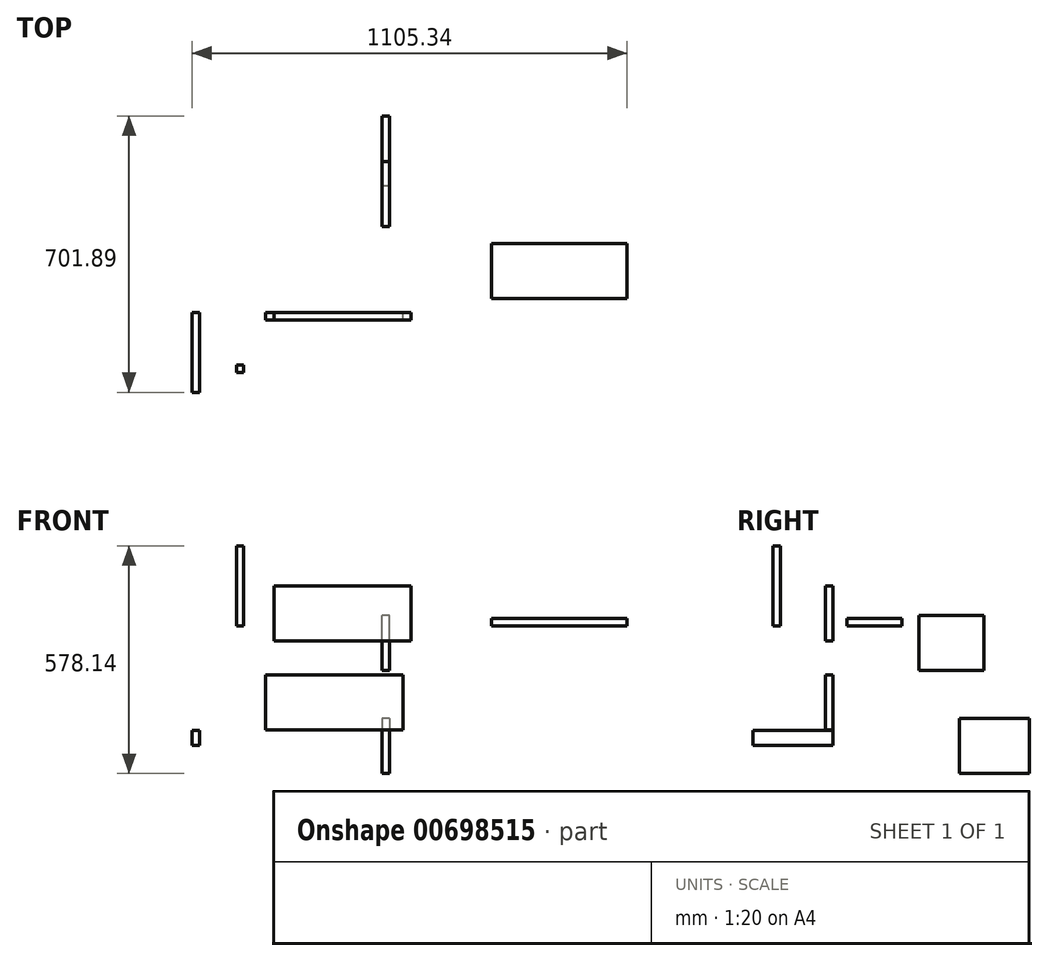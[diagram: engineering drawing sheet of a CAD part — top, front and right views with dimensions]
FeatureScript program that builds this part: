
annotation { "Feature Type Name" : "Feature", "Feature Type Description" : "" }
export const myFeature = defineFeature(function(context is Context, id is Id, definition is map)
    precondition{}
    {
        {
            var Q0;
            Q0=qCreatedBy(makeId("Front.planeOp"),FACE);
            var sketch = newSketch(context, id + "F0", { "sketchPlane" : qUnion([Q0])});
            skLineSegment(sketch, "E0.bottom", {"start": v(-274.43, 101.19) * mm, "end": v(74.34, 101.19) * mm});
            skLineSegment(sketch, "E0.top", {"start": v(-274.43, -38.51) * mm, "end": v(74.34, -38.51) * mm});
            skLineSegment(sketch, "E0.left", {"start": v(-274.43, 101.19) * mm, "end": v(-274.43, -38.51) * mm});
            skLineSegment(sketch, "E0.right", {"start": v(74.34, 101.19) * mm, "end": v(74.34, -38.51) * mm});
            skSolve(sketch);
        }
        {
            var Q0;
            Q0=makeQuery(id+"F0.imprint","IMPRINT",FACE,{"disambiguationData":[TD([[makeQuery(id+"F0.imprint","IMPRINT",EDGE,{"derivedFrom":sQuery(id+"F0.wireOp",EDGE,"E0.bottom")}),-1.0]])]});
            extrude(context, id + "F1", {"entities" : qUnion([Q0]), "depth" : 19.05 * mm, "offsetDistance" : 25.4 * mm});
        }
        {
            var Q0;
            Q0=qCreatedBy(makeId("Front.planeOp"),FACE);
            var sketch = newSketch(context, id + "F2", { "sketchPlane" : qUnion([Q0])});
            skLineSegment(sketch, "E1.bottom", {"start": v(-295.47, -125.17) * mm, "end": v(53.05, -125.17) * mm});
            skLineSegment(sketch, "E1.top", {"start": v(-295.47, -264.87) * mm, "end": v(53.05, -264.87) * mm});
            skLineSegment(sketch, "E1.left", {"start": v(-295.47, -125.17) * mm, "end": v(-295.47, -264.87) * mm});
            skLineSegment(sketch, "E1.right", {"start": v(53.05, -125.17) * mm, "end": v(53.05, -264.87) * mm});
            skSolve(sketch);
        }
        {
            var Q0;
            Q0=makeQuery(id+"F2.imprint","IMPRINT",FACE,{"disambiguationData":[TD([[makeQuery(id+"F2.imprint","IMPRINT",EDGE,{"derivedFrom":sQuery(id+"F2.wireOp",EDGE,"E1.bottom")}),-1.0]])]});
            extrude(context, id + "F3", {"entities" : qUnion([Q0]), "depth" : 19.05 * mm, "offsetDistance" : 25.4 * mm});
        }
        {
            var Q0;
            Q0=qCreatedBy(makeId("Right.planeOp"),FACE);
            var sketch = newSketch(context, id + "F4", { "sketchPlane" : qUnion([Q0])});
            skLineSegment(sketch, "E2.bottom", {"start": v(382.96, -112.78) * mm, "end": v(217.52, -112.78) * mm});
            skLineSegment(sketch, "E2.top", {"start": v(382.96, 26.92) * mm, "end": v(217.52, 26.92) * mm});
            skLineSegment(sketch, "E2.left", {"start": v(382.96, -112.78) * mm, "end": v(382.96, 26.92) * mm});
            skLineSegment(sketch, "E2.right", {"start": v(217.52, -112.78) * mm, "end": v(217.52, 26.92) * mm});
            skSolve(sketch);
        }
        {
            var Q0;
            Q0=makeQuery(id+"F4.imprint","IMPRINT",FACE,{"disambiguationData":[TD([[makeQuery(id+"F4.imprint","IMPRINT",EDGE,{"derivedFrom":sQuery(id+"F4.wireOp",EDGE,"E2.bottom")}),-1.0]])]});
            extrude(context, id + "F5", {"entities" : qUnion([Q0]), "depth" : 19.05 * mm, "offsetDistance" : 25.4 * mm});
        }
        {
            var Q0;
            Q0=qCreatedBy(makeId("Right.planeOp"),FACE);
            var sketch = newSketch(context, id + "F6", { "sketchPlane" : qUnion([Q0])});
            skLineSegment(sketch, "E3.bottom", {"start": v(321.18, -235.24) * mm, "end": v(498.69, -235.24) * mm});
            skLineSegment(sketch, "E3.top", {"start": v(321.18, -374.94) * mm, "end": v(498.69, -374.94) * mm});
            skLineSegment(sketch, "E3.left", {"start": v(321.18, -235.24) * mm, "end": v(321.18, -374.94) * mm});
            skLineSegment(sketch, "E3.right", {"start": v(498.69, -235.24) * mm, "end": v(498.69, -374.94) * mm});
            skSolve(sketch);
        }
        {
            var Q0;
            Q0=makeQuery(id+"F6.imprint","IMPRINT",FACE,{"disambiguationData":[TD([[makeQuery(id+"F6.imprint","IMPRINT",EDGE,{"derivedFrom":sQuery(id+"F6.wireOp",EDGE,"E3.bottom")}),-1.0]])]});
            extrude(context, id + "F7", {"entities" : qUnion([Q0]), "depth" : 19.05 * mm, "offsetDistance" : 25.4 * mm});
        }
        {
            var Q0;
            Q0=qCreatedBy(makeId("Top.planeOp"),FACE);
            var sketch = newSketch(context, id + "F8", { "sketchPlane" : qUnion([Q0])});
            skLineSegment(sketch, "E4.bottom", {"start": v(-369.84, -133.14) * mm, "end": v(-350.8, -133.14) * mm});
            skLineSegment(sketch, "E4.top", {"start": v(-369.84, -152.3) * mm, "end": v(-350.8, -152.3) * mm});
            skLineSegment(sketch, "E4.left", {"start": v(-369.84, -133.14) * mm, "end": v(-369.84, -152.3) * mm});
            skLineSegment(sketch, "E4.right", {"start": v(-350.8, -133.14) * mm, "end": v(-350.8, -152.3) * mm});
            skSolve(sketch);
        }
        {
            var Q0;
            Q0=makeQuery(id+"F8.imprint","IMPRINT",FACE,{"disambiguationData":[TD([[makeQuery(id+"F8.imprint","IMPRINT",EDGE,{"derivedFrom":sQuery(id+"F8.wireOp",EDGE,"E4.bottom")}),-1.0]])]});
            extrude(context, id + "F9", {"entities" : qUnion([Q0]), "depth" : 203.2 * mm, "offsetDistance" : 25.4 * mm});
        }
        {
            var Q0;
            Q0=qCreatedBy(makeId("Front.planeOp"),FACE);
            var sketch = newSketch(context, id + "F10", { "sketchPlane" : qUnion([Q0])});
            skLineSegment(sketch, "E5.bottom", {"start": v(-482.32, -265.36) * mm, "end": v(-463.27, -265.36) * mm});
            skLineSegment(sketch, "E5.top", {"start": v(-482.32, -304.09) * mm, "end": v(-463.27, -304.09) * mm});
            skLineSegment(sketch, "E5.left", {"start": v(-482.32, -265.36) * mm, "end": v(-482.32, -304.09) * mm});
            skLineSegment(sketch, "E5.right", {"start": v(-463.27, -265.36) * mm, "end": v(-463.27, -304.09) * mm});
            skSolve(sketch);
        }
        {
            var Q0;
            Q0 = qSketchRegion(id + "F10", true);
            extrude(context, id + "F11", {"entities" : qUnion([Q0]), "depth" : 203.2 * mm, "offsetDistance" : 25.4 * mm});
        }
        {
            var Q0;
            Q0=qCreatedBy(makeId("Top.planeOp"),FACE);
            var sketch = newSketch(context, id + "F12", { "sketchPlane" : qUnion([Q0])});
            skLineSegment(sketch, "E6.bottom", {"start": v(278.43, 174.56) * mm, "end": v(623.02, 174.56) * mm});
            skLineSegment(sketch, "E6.top", {"start": v(278.43, 34.86) * mm, "end": v(623.02, 34.86) * mm});
            skLineSegment(sketch, "E6.left", {"start": v(278.43, 174.56) * mm, "end": v(278.43, 34.86) * mm});
            skLineSegment(sketch, "E6.right", {"start": v(623.02, 174.56) * mm, "end": v(623.02, 34.86) * mm});
            skLineSegment(sketch, "E7.0", {"start": v(762.72, 174.56) * mm, "end": v(762.72, 34.86) * mm});
            skSolve(sketch);
        }
        {
            var Q0;
            Q0 = qSketchRegion(id + "F12", true);
            extrude(context, id + "F13", {"entities" : qUnion([Q0]), "depth" : 19.05 * mm, "offsetDistance" : 25.4 * mm});
        }
    });
